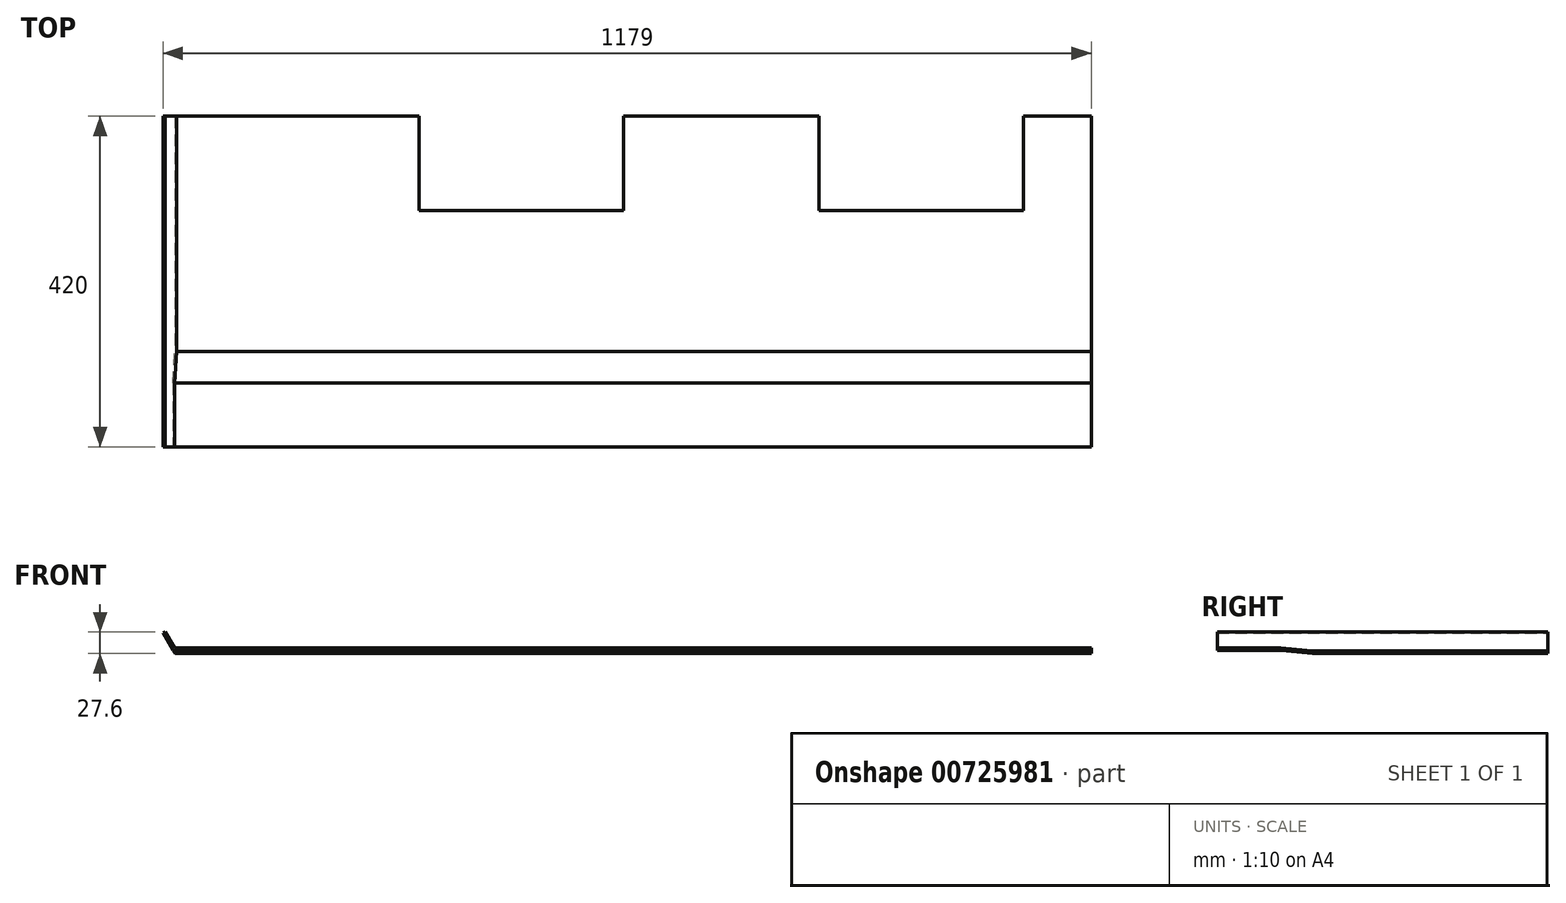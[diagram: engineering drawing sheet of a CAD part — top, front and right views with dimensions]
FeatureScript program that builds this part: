
annotation { "Feature Type Name" : "Feature", "Feature Type Description" : "" }
export const myFeature = defineFeature(function(context is Context, id is Id, definition is map)
    precondition{}
    {
        {
            var Q0;
            Q0=qCreatedBy(makeId("Right.planeOp"),FACE);
            var sketch = newSketch(context, id + "F0", { "sketchPlane" : qUnion([Q0])});
            skLineSegment(sketch, "E0", {"start": v(121, 0) * mm, "end": v(420, 0) * mm});
            skLineSegment(sketch, "E1.0", {"start": v(0, 4) * mm, "end": v(81, 4) * mm});
            skLineSegment(sketch, "E2.0", {"start": v(0, 7.2) * mm, "end": v(81.16, 7.2) * mm});
            skLineSegment(sketch, "E3", {"start": v(0, 4) * mm, "end": v(0, 7.2) * mm});
            skLineSegment(sketch, "E4", {"start": v(121, 0) * mm, "end": v(81, 4) * mm});
            skLineSegment(sketch, "E5.0", {"start": v(121.16, 3.2) * mm, "end": v(81.16, 7.2) * mm});
            skLineSegment(sketch, "E6.0", {"start": v(121.16, 3.2) * mm, "end": v(420, 3.2) * mm});
            skLineSegment(sketch, "E7", {"start": v(420, 0) * mm, "end": v(420, 3.2) * mm});
            skSolve(sketch);
        }
        {
            var Q0;
            Q0 = qSketchRegion(id + "F0", true);
            extrude(context, id + "F1", {"entities" : qUnion([Q0]), "depth" : 1179 * mm, "offsetDistance" : 25 * mm});
        }
        {
            var Q0;
            Q0=makeQuery(id+"F1.opExtrude","SWEPT_FACE",FACE,{"disambiguationData":[OSD([sQuery(id+"F0.wireOp",EDGE,"E6.0")])]});
            var sketch = newSketch(context, id + "F2", { "sketchPlane" : qUnion([Q0])});
            skLineSegment(sketch, "E8.bottom", {"start": v(1093, 420) * mm, "end": v(833, 420) * mm});
            skLineSegment(sketch, "E8.top", {"start": v(1093, 300) * mm, "end": v(833, 300) * mm});
            skLineSegment(sketch, "E8.left", {"start": v(1093, 420) * mm, "end": v(1093, 300) * mm});
            skLineSegment(sketch, "E8.right", {"start": v(833, 420) * mm, "end": v(833, 300) * mm});
            skLineSegment(sketch, "E9.bottom", {"start": v(585, 420) * mm, "end": v(325, 420) * mm});
            skLineSegment(sketch, "E9.top", {"start": v(585, 300) * mm, "end": v(325, 300) * mm});
            skLineSegment(sketch, "E9.left", {"start": v(585, 420) * mm, "end": v(585, 300) * mm});
            skLineSegment(sketch, "E9.right", {"start": v(325, 420) * mm, "end": v(325, 300) * mm});
            skSolve(sketch);
        }
        {
            var Q0;
            Q0=makeQuery(id+"F2.imprint","IMPRINT",FACE,{"disambiguationData":[TD([[makeQuery(id+"F2.imprint","IMPRINT",EDGE,{"derivedFrom":sQuery(id+"F2.wireOp",EDGE,"E9.bottom")}),1.0]])]});
            var Q1;
            Q1=makeQuery(id+"F2.imprint","IMPRINT",FACE,{"disambiguationData":[TD([[makeQuery(id+"F2.imprint","IMPRINT",EDGE,{"derivedFrom":sQuery(id+"F2.wireOp",EDGE,"E8.bottom")}),1.0]])]});
            extrude(context, id + "F3", {"entities" : qUnion([Q0, Q1]), "operationType" : NewBodyOperationType.REMOVE, "oppositeDirection" : true, "depth" : 25 * mm, "offsetDistance" : 25 * mm});
        }
        {
            var Q0;
            {var subQ1=sQuery(id+"F0.wireOp",EDGE,"E7");Q0=makeQuery(id+"F3.boolean.opBoolean","SPLIT",FACE,{"disambiguationData":[TD([makeQuery(id+"F3.opExtrude","SWEPT_FACE",FACE,{"disambiguationData":[OSD([sQuery(id+"F2.wireOp",EDGE,"E9.right")])]})])],"derivedFrom":makeQuery(id+"F1.opExtrude","SWEPT_FACE",FACE,{"disambiguationData":[OSD([subQ1])]})});}
            var sketch = newSketch(context, id + "F4", { "sketchPlane" : qUnion([Q0])});
            skLineSegment(sketch, "E10", {"start": v(-15, 0) * mm, "end": v(0, 26) * mm});
            skLineSegment(sketch, "E11.0", {"start": v(-17.77, 1.6) * mm, "end": v(-2.77, 27.6) * mm});
            skLineSegment(sketch, "E12", {"start": v(-2.77, 27.6) * mm, "end": v(0, 26) * mm});
            skLineSegment(sketch, "E13", {"start": v(-15, 0) * mm, "end": v(-17.77, 1.6) * mm});
            skSolve(sketch);
        }
        {
            var Q0;
            Q0 = qSketchRegion(id + "F4", true);
            extrude(context, id + "F5", {"entities" : qUnion([Q0]), "operationType" : NewBodyOperationType.ADD, "oppositeDirection" : true, "depth" : 420 * mm, "offsetDistance" : 25 * mm});
        }
        {
            var Q0;
            Q0=makeQuery(id+"F5.boolean.opBoolean","MERGE",FACE,{"derivedFrom":[makeQuery(id+"F1.opExtrude","SWEPT_FACE",FACE,{"disambiguationData":[OSD([sQuery(id+"F0.wireOp",EDGE,"E3")])]}),makeQuery(id+"F5.opExtrude","CAP_FACE",FACE,{"disambiguationData":[OSD([sQuery(id+"F4.wireOp",EDGE,"E10"),sQuery(id+"F4.wireOp",EDGE,"E11.0"),sQuery(id+"F4.wireOp",EDGE,"E12"),sQuery(id+"F4.wireOp",EDGE,"E13")])],"isStart":false})]});
            var sketch = newSketch(context, id + "F6", { "sketchPlane" : qUnion([Q0])});
            skLineSegment(sketch, "E14", {"start": v(10.85, 7.2) * mm, "end": v(15, 0) * mm});
            skLineSegment(sketch, "E15", {"start": v(15, 0) * mm, "end": v(0, 0) * mm});
            skLineSegment(sketch, "E16", {"start": v(0, 0) * mm, "end": v(0, 7.2) * mm});
            skLineSegment(sketch, "E17", {"start": v(0, 7.2) * mm, "end": v(10.85, 7.2) * mm});
            skSolve(sketch);
        }
        {
            var Q0;
            {var subQ0=sQuery(id+"F6.wireOp",EDGE,"E15");Q0=makeQuery(id+"F6.imprint","IMPRINT",FACE,{"disambiguationData":[TD([[makeQuery(id+"F6.imprint","IMPRINT",EDGE,{"derivedFrom":subQ0}),-1.0]])]});}
            var Q1;
            {var subQ10=sQuery(id+"F6.wireOp",EDGE,"E17");Q1=makeQuery(id+"F6.imprint","IMPRINT",FACE,{"disambiguationData":[TD([[makeQuery(id+"F6.imprint","IMPRINT",EDGE,{"derivedFrom":subQ10}),1.0]])]});}
            extrude(context, id + "F7", {"entities" : qUnion([Q0, Q1]), "operationType" : NewBodyOperationType.REMOVE, "oppositeDirection" : true, "depth" : 420 * mm, "offsetDistance" : 25 * mm});
        }
        {
            var Q0;
            Q0=makeQuery(id+"F1.opExtrude","CAP_FACE",FACE,{"disambiguationData":[OSD([sQuery(id+"F0.wireOp",EDGE,"E0"),sQuery(id+"F0.wireOp",EDGE,"E1.0"),sQuery(id+"F0.wireOp",EDGE,"E2.0"),sQuery(id+"F0.wireOp",EDGE,"E3"),sQuery(id+"F0.wireOp",EDGE,"E4"),sQuery(id+"F0.wireOp",EDGE,"E5.0"),sQuery(id+"F0.wireOp",EDGE,"E6.0"),sQuery(id+"F0.wireOp",EDGE,"E7")])],"isStart":false});
            var sketch = newSketch(context, id + "F8", { "sketchPlane" : qUnion([Q0])});
            skLineSegment(sketch, "E18", {"start": v(0, 4) * mm, "end": v(81, 4) * mm});
            skLineSegment(sketch, "E19", {"start": v(81, 4) * mm, "end": v(121, 0) * mm});
            skLineSegment(sketch, "E20", {"start": v(121, 0) * mm, "end": v(0, 0) * mm});
            skLineSegment(sketch, "E21", {"start": v(0, 0) * mm, "end": v(0, 4) * mm});
            skSolve(sketch);
        }
        {
            var Q0;
            Q0=makeQuery(id+"F8.imprint","IMPRINT",FACE,{"disambiguationData":[TD([[makeQuery(id+"F8.imprint","IMPRINT",EDGE,{"derivedFrom":sQuery(id+"F8.wireOp",EDGE,"E18")}),-1.0]])]});
            extrude(context, id + "F9", {"entities" : qUnion([Q0]), "operationType" : NewBodyOperationType.REMOVE, "oppositeDirection" : true, "depth" : 1200 * mm, "offsetDistance" : 25 * mm});
        }
    });
